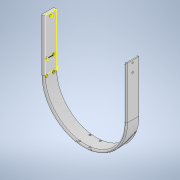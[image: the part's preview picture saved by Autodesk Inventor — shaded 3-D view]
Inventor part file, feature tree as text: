
AUTODESK INVENTOR PART (.ipt)
format: ipt  version: 2022 (Build 260153000, 153)  size: 586,752 bytes
history: native  units: in
note: dims shown in document units (in); Inventor stores cm internally (conversion verified against a paired STEP export)
features: sketch x23, extrude x23, projected_geometry x22, plane x3, fillet x2, mirror x1
ambient origin geometry x8: Origin, YZ Plane, XZ Plane, XY Plane, X Axis, Y Axis, Z Axis, Center Point
bodies: Solid1 (feature_tree)
feature tree (74):
  sketch  "Sketch1"  dims[d0=9.2in d1=0.2in]
  extrude  "Extrusion1"  Depth=0.2in
  extrude  "Extrusion2"  Depth=1.0in TaperAngle=0.0deg
  sketch  "Sketch3"  dims[d6=1.35in d7=0.12in]
  extrude  "Extrusion3"  Depth=0.12in
  extrude  "Extrusion4"  Depth=0.12in
  sketch  "Sketch4"  dims[d8=0.12in d9=0.12in]
  extrude  "Extrusion5"  Depth=1.15in
  extrude  "Extrusion6"  Depth=0.226in
  extrude  "Extrusion7"  Depth=1.5in TaperAngle=0.0deg
  sketch  "Sketch6"  dims[d12=0.1in d13=0.226in]
  plane  "Work Plane1"
  sketch  "Sketch7"  dims[d14=1.0in d15=0.0in d16=1.5in d17=0.0in]
  extrude  "Extrusion8"  Depth=1.5in TaperAngle=0.0deg
  extrude  "Extrusion9"  Depth=1.3in
  extrude  "Extrusion10"  Depth=0.475in
  sketch  "Sketch9"  dims[d22=0.66in d23=1.3in]
  sketch  "Sketch10"  dims[d24=0.26in d25=0.475in]
  extrude  "Extrusion11"  Depth=0.13in
  extrude  "Extrusion12"  Depth=0.12in
  extrude  "Extrusion13"  Depth=0.175in
  extrude  "Extrusion14"  Depth=1.5in TaperAngle=0.0deg
  extrude  "Extrusion15"  Depth=0.12in
  extrude  "Extrusion16"  Depth=0.4in
  extrude  "Extrusion17"  Depth=0.12in
  sketch  "Sketch15"  dims[d35=0.12in d36=0.12in]
  extrude  "Extrusion18"  Depth=0.1in
  sketch  "Sketch16"  dims[d37=0.4in d38=0.4in]
  fillet  "Fillet1"  Radius=1.5in
  extrude  "Extrusion19"  Depth=0.2in
  fillet  "Fillet2"  Radius=1.0in
  plane  "Work Plane2"
  extrude  "Extrusion22"  Depth=0.475in
  sketch  "Sketch19"  dims[d45=1.5in d46=0.2in d47=1.0in d48=0.0in]
  plane  "Work Plane3"
  extrude  "Extrusion23"  Depth=1.3in
  mirror  "Mirror1"
  sketch  "Sketch21"  dims[d52=0.26in d53=1.3in]
  extrude  "Extrusion24"  Depth=0.31in
  extrude  "Extrusion25"  Depth=0.12in
  sketch  "Sketch2"  dims[d2=1.0in d3=0.0in d4=1.0in d5=0.0in]
  projected_geometry  "Projected Loop1"
  projected_geometry  "Projected Loop2"
  projected_geometry  "Projected Loop3"
  sketch  "Sketch5"  dims[d10=0.12in d11=1.15in]
  projected_geometry  "Projected Loop4"
  projected_geometry  "Projected Loop5"
  projected_geometry  "Projected Loop6"
  sketch  "Sketch8"  dims[d18=1.5in d19=0.0in d20=1.5in d21=0.0in]
  projected_geometry  "Projected Loop7"
  projected_geometry  "Projected Loop8"
  projected_geometry  "Projected Loop9"
  projected_geometry  "Projected Loop10"
  sketch  "Sketch11"  dims[d26=0.31in d27=0.13in]
  projected_geometry  "Projected Loop11"
  sketch  "Sketch12"  dims[d28=1.0in d29=0.12in]
  sketch  "Sketch13"  dims[d30=0.12in d31=0.175in]
  projected_geometry  "Projected Loop12"
  projected_geometry  "Projected Loop13"
  projected_geometry  "Projected Loop14"
  projected_geometry  "Projected Loop15"
  projected_geometry  "Projected Loop16"
  sketch  "Sketch14"  dims[d32=0.175in d33=1.5in d34=0.0in]
  projected_geometry  "Projected Loop17"
  projected_geometry  "Projected Loop18"
  sketch  "Sketch17"  dims[d39=0.1in d40=0.12in]
  projected_geometry  "Projected Loop19"
  sketch  "Sketch18"  dims[d41=0.12in d42=0.1in d43=1.5in d44=0.0in]
  projected_geometry  "Projected Loop20"
  projected_geometry  "Projected Loop21"
  sketch  "Sketch20"  dims[d49=4.0in d50=0.0in d51=0.475in]
  projected_geometry  "Projected Loop22"
  sketch  "Sketch22"  dims[d54=0.13in d55=0.31in]
  sketch  "Sketch23"  dims[d56=0.66in d57=0.12in d58=0.1in d59=0.12in d60=0.12in d61=0.12in d62=1.15in d63=3.0in d64=0.0in d65=0.2in d66=0.0in d67=29.0in d68=0.0in d69=0.12in d70=0.175in d71=0.12in d72=0.65in d73=2.0in d74=0.0in d75=2.0in d76=0.0in d77=1.0in d78=0.0in d79=0.8661in d80=0.12in d81=0.12in d82=1.15in d83=0.12in d84=0.12in d85=2.0in d86=0.0in d87=1.0in d88=0.0in d89=0.125in d90=0.12in d91=0.25in d92=1.0in d93=0.0in d94=0.125in d95=0.0787in d100=0.1969in d101=0.0in d102=1.825in d103=0.65in d104=0.292in d105=0.0787in d106=0.0984in d107=0.0in d108=0.2236in d109=0.2236in d110=0.1181in d111=0.0in d112=0.2236in d113=0.2236in d114=0.2236in d115=0.2236in d116=0.2236in d117=0.2362in d118=0.0in]
